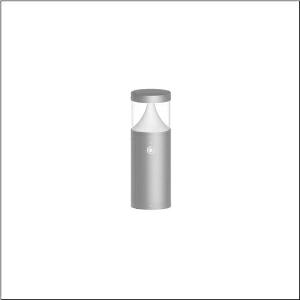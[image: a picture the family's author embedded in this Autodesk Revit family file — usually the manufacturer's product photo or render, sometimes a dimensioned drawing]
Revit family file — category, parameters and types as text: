
# Revit family: cl_31_poller_40_sensor_5cl424803
name_source: partatom
category: Lighting Fixtures
units: mm (PartAtom-declared; Revit-internal decimal feet)

## family parameters
Cut with Voids When Loaded = No
Host = Face
Light Source = No
Part Type = Normal
Room Calculation Point = No
Round Connector Dimension = Use Diameter
Shared = No

## types (1)
- --- (1 x LED, 800 lm, 7.2 W, 3000K)
    Apparent Load = 7 VA
    CIE Flux Codes = 19 66 88 92 100
    Color Rendering = 80
    Color Temperature = 3000K
    Default Elevation = 1800 mm
    Description = CL 31 Bollard 40 Sensor, bollard luminaire, primary light control with lens, of PC, primary optical cover: cover panel, of PC, transparent, secondary light control with reflector, of PC, primary light characteristic: asymmetric, LED, rated luminous flux: 800lm, luminous efficacy: 110lm/W, light colour: 830, colour temperature: 3000K, control gear: ECG DALI, with terminal, 5-pole, max. 2.5mm², mains connection: 220..240V, AC, 50/60Hz, rated input power: 7.2W, luminaire housing, of aluminium, powder-coated, Siteco® metallic grey, diameter: 170mm, height: 400mm, PIR sensor, protection rating (complete): IP65, insulation class (complete): insulation class I (protective earthing), certification: CE, ENEC, impact resistance: IK08, permissible operating ambient temperature for outdoor applications: -20..+50°C, packaging unit: 1 piece
    Height = 200 mm
    Lamp = 1 x LED
    Lamp Light Flux = 800 lm
    Lamp Power = 7.2 W
    Lamp count = 1
    Length = 170 mm
    Luminous efficacy = 111 lm/W
    Manufacturer = Siteco
    ModVariant = No
    Model = 5CL424803
    Mounting Place = Floor
    Mounting Type = Freestanding
    Number of Poles = 1
    OnlyDefault = Yes
    Power Factor = 1
    Product Name = CL 31 Poller 40 Sensor
    Product group = bollard luminaire
    ProductGroupID = 1304
    Protection Class = Protection class I
    Protection Degree = IP 65
    RLX_Detail_Level = 1
    RLX_Emergency_Light_Flux = 0 lm
    RLX_Emergency_Type = 0
    RLX_Emergency_Type_DB = No
    RlxData = <blob elided: 62413 chars, md5=ad072f2f>
    Socket = socket
    Standby Power = 0 W
    System Light Flux = 800 lm
    System Power = 7 W
    Type Comments = factory setting: luminous flux: 100 % | dim-lin: 254 | 182 mA
    Type Image = l_1006905.jpg
    URL = http://relux.com
    VarID = @adj_148301
    Voltage = 0 V
    Weight = 0.00 kg
    Width = 0 mm  [stored 0 ft]

note: [stored X ft] marks values corroborated as IEEE doubles in the binary element streams (Revit-internal decimal feet)

## geometry (parser evidence)
native form markers: Blend x4, Sweep x13
no freeform markers — native parametric forms only
